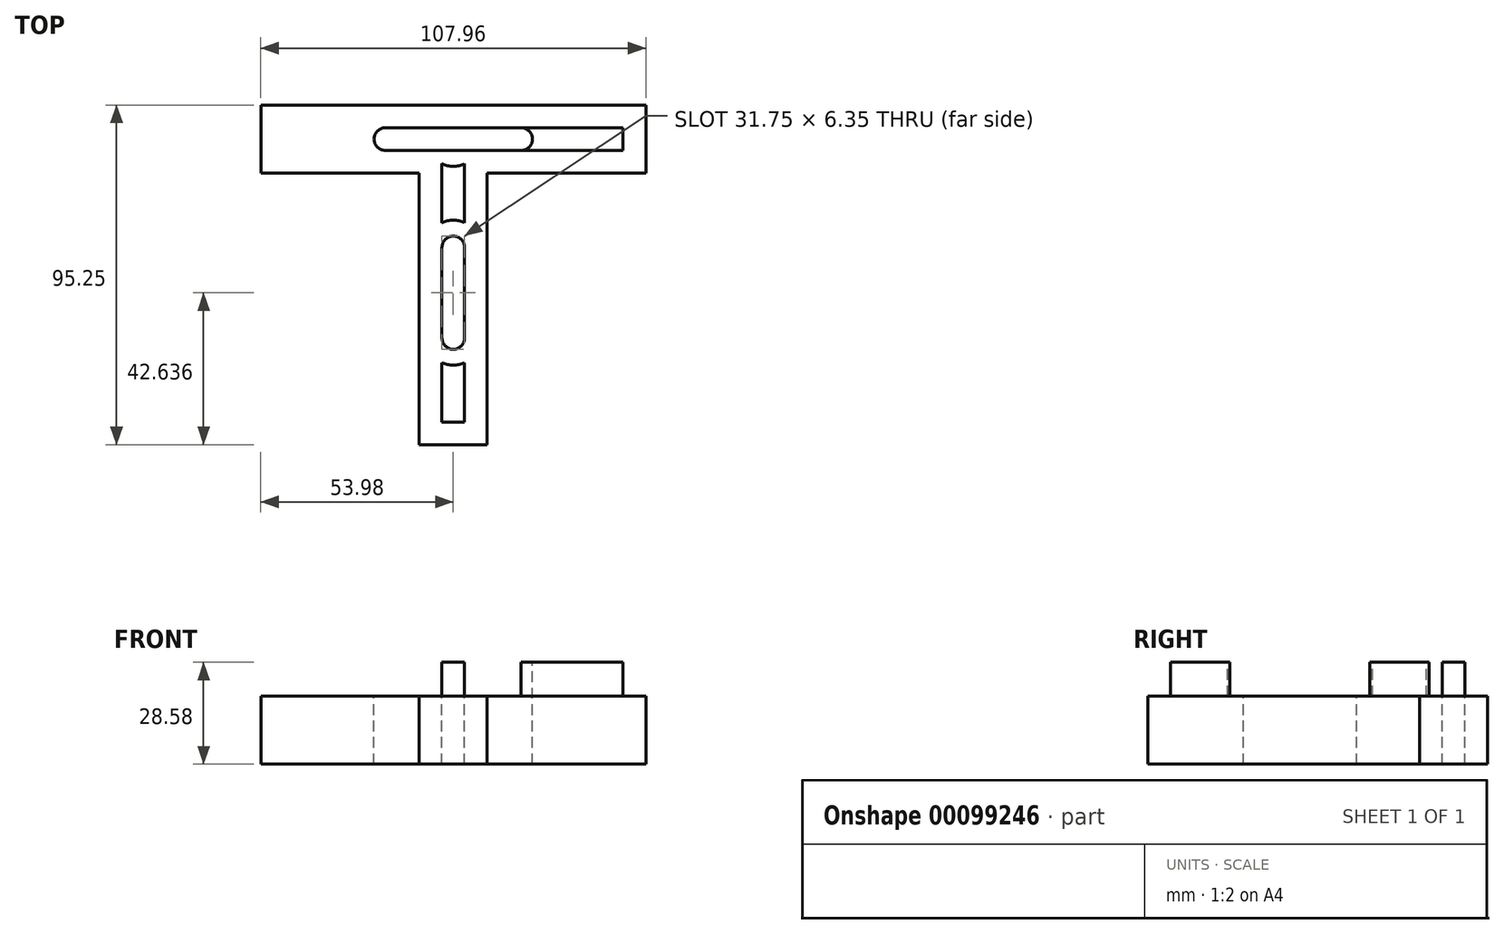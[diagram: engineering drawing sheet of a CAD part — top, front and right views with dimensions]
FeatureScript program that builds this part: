
annotation { "Feature Type Name" : "Feature", "Feature Type Description" : "" }
export const myFeature = defineFeature(function(context is Context, id is Id, definition is map)
    precondition{}
    {
        {
            var Q0;
            Q0=qCreatedBy(makeId("Top.planeOp"),FACE);
            var sketch = newSketch(context, id + "F0", { "sketchPlane" : qUnion([Q0])});
            skLineSegment(sketch, "E0", {"start": v(0, 0) * mm, "end": v(0, -76.2) * mm, "construction": true});
            skLineSegment(sketch, "E1", {"start": v(-44.45, 0) * mm, "end": v(44.45, 0) * mm, "construction": true});
            skLineSegment(sketch, "E2", {"start": v(0, 9.53) * mm, "end": v(53.97, 9.53) * mm});
            skLineSegment(sketch, "E3", {"start": v(53.97, 9.53) * mm, "end": v(53.97, -9.52) * mm});
            skLineSegment(sketch, "E4", {"start": v(53.97, -9.52) * mm, "end": v(9.52, -9.53) * mm});
            skLineSegment(sketch, "E5", {"start": v(9.52, -9.52) * mm, "end": v(9.53, -85.73) * mm});
            skLineSegment(sketch, "E6", {"start": v(9.53, -85.73) * mm, "end": v(0, -85.73) * mm});
            skLineSegment(sketch, "E7.MirrorCS", {"start": v(-9.52, -9.52) * mm, "end": v(-9.53, -85.73) * mm});
            skLineSegment(sketch, "E8.MirrorCS", {"start": v(-9.53, -85.73) * mm, "end": v(0, -85.73) * mm});
            skLineSegment(sketch, "E9.MirrorCS", {"start": v(-53.97, -9.52) * mm, "end": v(-9.52, -9.53) * mm});
            skLineSegment(sketch, "E10.MirrorCS", {"start": v(-53.97, 9.53) * mm, "end": v(-53.97, -9.52) * mm});
            skLineSegment(sketch, "E11.MirrorCS", {"start": v(0, 9.53) * mm, "end": v(-53.97, 9.53) * mm});
            skSolve(sketch);
        }
        {
            var Q0;
            Q0=makeQuery(id+"F0.imprint","IMPRINT",FACE,{"disambiguationData":[TD([[makeQuery(id+"F0.imprint","IMPRINT",EDGE,{"derivedFrom":sQuery(id+"F0.wireOp",EDGE,"E2")}),-1.0]])]});
            extrude(context, id + "F1", {"entities" : qUnion([Q0]), "depth" : 19.05 * mm});
        }
        {
            var Q0;
            Q0=makeQuery(id+"F1.opExtrude","CAP_FACE",FACE,{"disambiguationData":[OSD([sQuery(id+"F0.wireOp",EDGE,"E2"),sQuery(id+"F0.wireOp",EDGE,"E3"),sQuery(id+"F0.wireOp",EDGE,"E4"),sQuery(id+"F0.wireOp",EDGE,"E5"),sQuery(id+"F0.wireOp",EDGE,"E6"),sQuery(id+"F0.wireOp",EDGE,"E7.MirrorCS"),sQuery(id+"F0.wireOp",EDGE,"E8.MirrorCS"),sQuery(id+"F0.wireOp",EDGE,"E9.MirrorCS"),sQuery(id+"F0.wireOp",EDGE,"E10.MirrorCS"),sQuery(id+"F0.wireOp",EDGE,"E11.MirrorCS")])],"isStart":false});
            var sketch = newSketch(context, id + "F2", { "sketchPlane" : qUnion([Q0])});
            skLineSegment(sketch, "E12.0", {"start": v(-47.62, 3.18) * mm, "end": v(-47.62, -3.17) * mm});
            skLineSegment(sketch, "E12.1", {"start": v(-47.62, -3.17) * mm, "end": v(-3.17, -3.18) * mm});
            skLineSegment(sketch, "E12.2", {"start": v(-47.62, 3.18) * mm, "end": v(47.62, 3.18) * mm});
            skLineSegment(sketch, "E12.3", {"start": v(-3.17, -3.18) * mm, "end": v(-3.18, -79.38) * mm});
            skLineSegment(sketch, "E12.4", {"start": v(47.62, 3.18) * mm, "end": v(47.62, -3.17) * mm});
            skLineSegment(sketch, "E12.5", {"start": v(47.62, -3.17) * mm, "end": v(3.17, -3.18) * mm});
            skLineSegment(sketch, "E12.6", {"start": v(3.17, -3.18) * mm, "end": v(3.18, -79.38) * mm});
            skLineSegment(sketch, "E12.7", {"start": v(-3.18, -79.38) * mm, "end": v(3.18, -79.38) * mm});
            skSolve(sketch);
        }
        {
            var Q0;
            Q0=makeQuery(id+"F2.imprint","IMPRINT",FACE,{"disambiguationData":[TD([[makeQuery(id+"F2.imprint","IMPRINT",EDGE,{"derivedFrom":sQuery(id+"F2.wireOp",EDGE,"E12.0")}),1.0]])]});
            extrude(context, id + "F3", {"entities" : qUnion([Q0]), "operationType" : NewBodyOperationType.ADD, "depth" : 9.52 * mm});
        }
        {
            var Q0;
            Q0=makeQuery(id+"F3.opExtrude","CAP_FACE",FACE,{"disambiguationData":[OSD([sQuery(id+"F2.wireOp",EDGE,"E12.0"),sQuery(id+"F2.wireOp",EDGE,"E12.1"),sQuery(id+"F2.wireOp",EDGE,"E12.2"),sQuery(id+"F2.wireOp",EDGE,"E12.3"),sQuery(id+"F2.wireOp",EDGE,"E12.4"),sQuery(id+"F2.wireOp",EDGE,"E12.5"),sQuery(id+"F2.wireOp",EDGE,"E12.6"),sQuery(id+"F2.wireOp",EDGE,"E12.7")])],"isStart":false});
            var sketch = newSketch(context, id + "F4", { "sketchPlane" : qUnion([Q0])});
            skLineSegment(sketch, "E13", {"start": v(0, -55.78) * mm, "end": v(0, -30.38) * mm, "construction": true});
            skArc(sketch, "E14.0.startCap", {"start": v(3.18, -55.78) * mm, "mid": v(0, -58.96) * mm, "end": v(-3.18, -55.78) * mm});
            skArc(sketch, "E14.0.endCap", {"start": v(-3.18, -30.38) * mm, "mid": v(0, -27.2) * mm, "end": v(3.18, -30.38) * mm});
            skLineSegment(sketch, "E14.0.left", {"start": v(-3.18, -55.78) * mm, "end": v(-3.18, -30.38) * mm});
            skLineSegment(sketch, "E14.0.right", {"start": v(3.18, -55.78) * mm, "end": v(3.18, -30.38) * mm});
            skLineSegment(sketch, "E15", {"start": v(0, 0) * mm, "end": v(19.05, 0) * mm, "construction": true});
            skLineSegment(sketch, "E16.MirrorCS", {"start": v(0, 0) * mm, "end": v(-19.05, 0) * mm, "construction": true});
            skArc(sketch, "E17.0.endCap", {"start": v(-19.05, -3.18) * mm, "mid": v(-22.23, 0) * mm, "end": v(-19.05, 3.18) * mm});
            skLineSegment(sketch, "E17.0.left", {"start": v(0, -3.18) * mm, "end": v(-19.05, -3.18) * mm});
            skLineSegment(sketch, "E17.0.right", {"start": v(0, 3.18) * mm, "end": v(-19.05, 3.18) * mm});
            skArc(sketch, "E17.1.endCap", {"start": v(19.05, 3.18) * mm, "mid": v(22.23, 0) * mm, "end": v(19.05, -3.18) * mm});
            skLineSegment(sketch, "E17.1.left", {"start": v(0, 3.18) * mm, "end": v(19.05, 3.18) * mm});
            skLineSegment(sketch, "E17.1.right", {"start": v(0, -3.18) * mm, "end": v(19.05, -3.18) * mm});
            skSolve(sketch);
        }
        {
            var Q0;
            Q0 = qSketchRegion(id + "F4", true);
            extrude(context, id + "F5", {"entities" : qUnion([Q0]), "operationType" : NewBodyOperationType.REMOVE, "endBound" : BoundingType.THROUGH_ALL, "oppositeDirection" : true, "depth" : 25.4 * mm});
        }
        {
            var Q0;
            {var subQ0=sQuery(id+"F2.wireOp",EDGE,"E12.0");var subQ1=sQuery(id+"F2.wireOp",EDGE,"E12.1");var subQ2=sQuery(id+"F2.wireOp",EDGE,"E12.2");Q0=makeQuery(id+"F5.boolean.opBoolean","SPLIT",FACE,{"disambiguationData":[TD([makeQuery(id+"F3.opExtrude","SWEPT_FACE",FACE,{"disambiguationData":[OSD([subQ0])]})])],"derivedFrom":makeQuery(id+"F3.opExtrude","CAP_FACE",FACE,{"disambiguationData":[OSD([subQ0,subQ1,subQ2,sQuery(id+"F2.wireOp",EDGE,"E12.3"),sQuery(id+"F2.wireOp",EDGE,"E12.4"),sQuery(id+"F2.wireOp",EDGE,"E12.5"),sQuery(id+"F2.wireOp",EDGE,"E12.6"),sQuery(id+"F2.wireOp",EDGE,"E12.7")])],"isStart":false})});}
            var sketch = newSketch(context, id + "F6", { "sketchPlane" : qUnion([Q0])});
            skCircle(sketch, "E18", {"center": v(-19.05, 0) * mm, "radius": 7.62 * mm});
            skCircle(sketch, "E19.MirrorC", {"center": v(19.05, 0) * mm, "radius": 7.62 * mm});
            skCircle(sketch, "E20", {"center": v(0, -30.38) * mm, "radius": 7.62 * mm});
            skCircle(sketch, "E21", {"center": v(0, -55.78) * mm, "radius": 7.62 * mm});
            skCircle(sketch, "E22", {"center": v(0, 0) * mm, "radius": 7.62 * mm});
            skSolve(sketch);
        }
        {
            var Q0;
            {var subQ6=sQuery(id+"F4.wireOp",EDGE,"E17.0.endCap");var subQ9=makeQuery(id+"F5.boolean.opBoolean","COPY",EDGE,{"derivedFrom":makeQuery(id+"F5.opExtrude","CAP_EDGE",EDGE,{"disambiguationData":[OSD([subQ6])],"isStart":true})});Q0=makeQuery(id+"F6.imprint","IMPRINT",FACE,{"disambiguationData":[TD([[makeQuery(id+"F6.imprint","IMPRINT",EDGE,{"derivedFrom":subQ9}),-1.0]])]});}
            var Q1;
            Q1=makeQuery(id+"F6.imprint","IMPRINT",FACE,{"disambiguationData":[TD([[makeQuery(id+"F6.imprint","IMPRINT",EDGE,{"derivedFrom":sQuery(id+"F6.wireOp",EDGE,"E19.MirrorC")}),-1.0]])]});
            var Q2;
            Q2=makeQuery(id+"F6.imprint","IMPRINT",FACE,{"disambiguationData":[TD([[makeQuery(id+"F6.imprint","IMPRINT",EDGE,{"derivedFrom":sQuery(id+"F6.wireOp",EDGE,"E20")}),1.0]])]});
            var Q3;
            Q3=makeQuery(id+"F6.imprint","IMPRINT",FACE,{"disambiguationData":[TD([[makeQuery(id+"F6.imprint","IMPRINT",EDGE,{"derivedFrom":sQuery(id+"F6.wireOp",EDGE,"E21")}),1.0]])]});
            var Q4;
            {var subQ6=sQuery(id+"F4.wireOp",EDGE,"E17.0.endCap");var subQ9=makeQuery(id+"F5.boolean.opBoolean","COPY",EDGE,{"derivedFrom":makeQuery(id+"F5.opExtrude","CAP_EDGE",EDGE,{"disambiguationData":[OSD([subQ6])],"isStart":true})});Q4=makeQuery(id+"F6.imprint","IMPRINT",FACE,{"disambiguationData":[TD([[makeQuery(id+"F6.imprint","IMPRINT",EDGE,{"derivedFrom":subQ9}),1.0]])]});}
            var Q5;
            Q5=makeQuery(id+"F6.imprint","IMPRINT",FACE,{"disambiguationData":[TD([[makeQuery(id+"F6.imprint","IMPRINT",EDGE,{"derivedFrom":sQuery(id+"F6.wireOp",EDGE,"E22")}),1.0]])]});
            extrude(context, id + "F7", {"entities" : qUnion([Q0, Q1, Q2, Q3, Q4, Q5]), "operationType" : NewBodyOperationType.REMOVE, "oppositeDirection" : true, "depth" : 9.52 * mm});
        }
        {
            var Q0;
            {var subQ0=sQuery(id+"F2.wireOp",EDGE,"E12.0");var subQ1=sQuery(id+"F2.wireOp",EDGE,"E12.1");var subQ2=sQuery(id+"F2.wireOp",EDGE,"E12.2");Q0=makeQuery(id+"F5.boolean.opBoolean","SPLIT",FACE,{"disambiguationData":[TD([makeQuery(id+"F3.opExtrude","SWEPT_FACE",FACE,{"disambiguationData":[OSD([subQ0])]})])],"derivedFrom":makeQuery(id+"F3.opExtrude","CAP_FACE",FACE,{"disambiguationData":[OSD([subQ0,subQ1,subQ2,sQuery(id+"F2.wireOp",EDGE,"E12.3"),sQuery(id+"F2.wireOp",EDGE,"E12.4"),sQuery(id+"F2.wireOp",EDGE,"E12.5"),sQuery(id+"F2.wireOp",EDGE,"E12.6"),sQuery(id+"F2.wireOp",EDGE,"E12.7")])],"isStart":false})});}
            var sketch = newSketch(context, id + "F8", { "sketchPlane" : qUnion([Q0])});
            skLineSegment(sketch, "E23.0", {"start": v(-47.62, 3.18) * mm, "end": v(-25.98, 3.18) * mm});
            skLineSegment(sketch, "E24.0", {"start": v(-47.62, 3.18) * mm, "end": v(-47.62, -3.17) * mm});
            skLineSegment(sketch, "E25.0", {"start": v(-47.62, -3.17) * mm, "end": v(-25.98, -3.18) * mm});
            skArc(sketch, "E26.0", {"start": v(-25.98, 3.17) * mm, "mid": v(-26.67, 0) * mm, "end": v(-25.98, -3.17) * mm});
            skArc(sketch, "E27.0", {"start": v(25.98, 3.17) * mm, "mid": v(26.67, 0) * mm, "end": v(25.98, -3.17) * mm});
            skLineSegment(sketch, "E28.0", {"start": v(25.98, 3.18) * mm, "end": v(47.62, 3.18) * mm});
            skLineSegment(sketch, "E29.0", {"start": v(47.62, 3.18) * mm, "end": v(47.62, -3.17) * mm});
            skLineSegment(sketch, "E30.0", {"start": v(47.62, -3.17) * mm, "end": v(25.98, -3.18) * mm});
            skSolve(sketch);
        }
        {
            var Q0;
            Q0=makeQuery(id+"F8.imprint","IMPRINT",FACE,{"disambiguationData":[TD([[makeQuery(id+"F8.imprint","IMPRINT",EDGE,{"derivedFrom":sQuery(id+"F8.wireOp",EDGE,"E23.0")}),-1.0]])]});
            var Q1;
            Q1=makeQuery(id+"F8.imprint","IMPRINT",FACE,{"disambiguationData":[TD([[makeQuery(id+"F8.imprint","IMPRINT",EDGE,{"derivedFrom":sQuery(id+"F8.wireOp",EDGE,"E27.0")}),1.0]])]});
            var Q2;
            Q2=makeQuery(id+"F7.boolean.opBoolean","MERGE",FACE,{"derivedFrom":[makeQuery(id+"F1.opExtrude","CAP_FACE",FACE,{"disambiguationData":[OSD([sQuery(id+"F0.wireOp",EDGE,"E2"),sQuery(id+"F0.wireOp",EDGE,"E3"),sQuery(id+"F0.wireOp",EDGE,"E4"),sQuery(id+"F0.wireOp",EDGE,"E5"),sQuery(id+"F0.wireOp",EDGE,"E6"),sQuery(id+"F0.wireOp",EDGE,"E7.MirrorCS"),sQuery(id+"F0.wireOp",EDGE,"E8.MirrorCS"),sQuery(id+"F0.wireOp",EDGE,"E9.MirrorCS"),sQuery(id+"F0.wireOp",EDGE,"E10.MirrorCS"),sQuery(id+"F0.wireOp",EDGE,"E11.MirrorCS")])],"isStart":false}),makeQuery(id+"F7.opExtrude","CAP_FACE",FACE,{"disambiguationData":[OSD([sQuery(id+"F6.wireOp",EDGE,"E18")])],"isStart":false}),makeQuery(id+"F7.opExtrude","CAP_FACE",FACE,{"disambiguationData":[OSD([sQuery(id+"F6.wireOp",EDGE,"E19.MirrorC")])],"isStart":false}),makeQuery(id+"F7.opExtrude","CAP_FACE",FACE,{"disambiguationData":[OSD([sQuery(id+"F6.wireOp",EDGE,"E20")])],"isStart":false}),makeQuery(id+"F7.opExtrude","CAP_FACE",FACE,{"disambiguationData":[OSD([sQuery(id+"F6.wireOp",EDGE,"E21")])],"isStart":false}),makeQuery(id+"F7.opExtrude","CAP_FACE",FACE,{"disambiguationData":[OSD([sQuery(id+"F6.wireOp",EDGE,"E22")])],"isStart":false})]});
            extrude(context, id + "F9", {"entities" : qUnion([Q0, Q1]), "operationType" : NewBodyOperationType.REMOVE, "endBound" : BoundingType.UP_TO_SURFACE, "oppositeDirection" : true, "endBoundEntityFace" : qUnion([Q2]), "depth" : 25.4 * mm});
        }
    });
